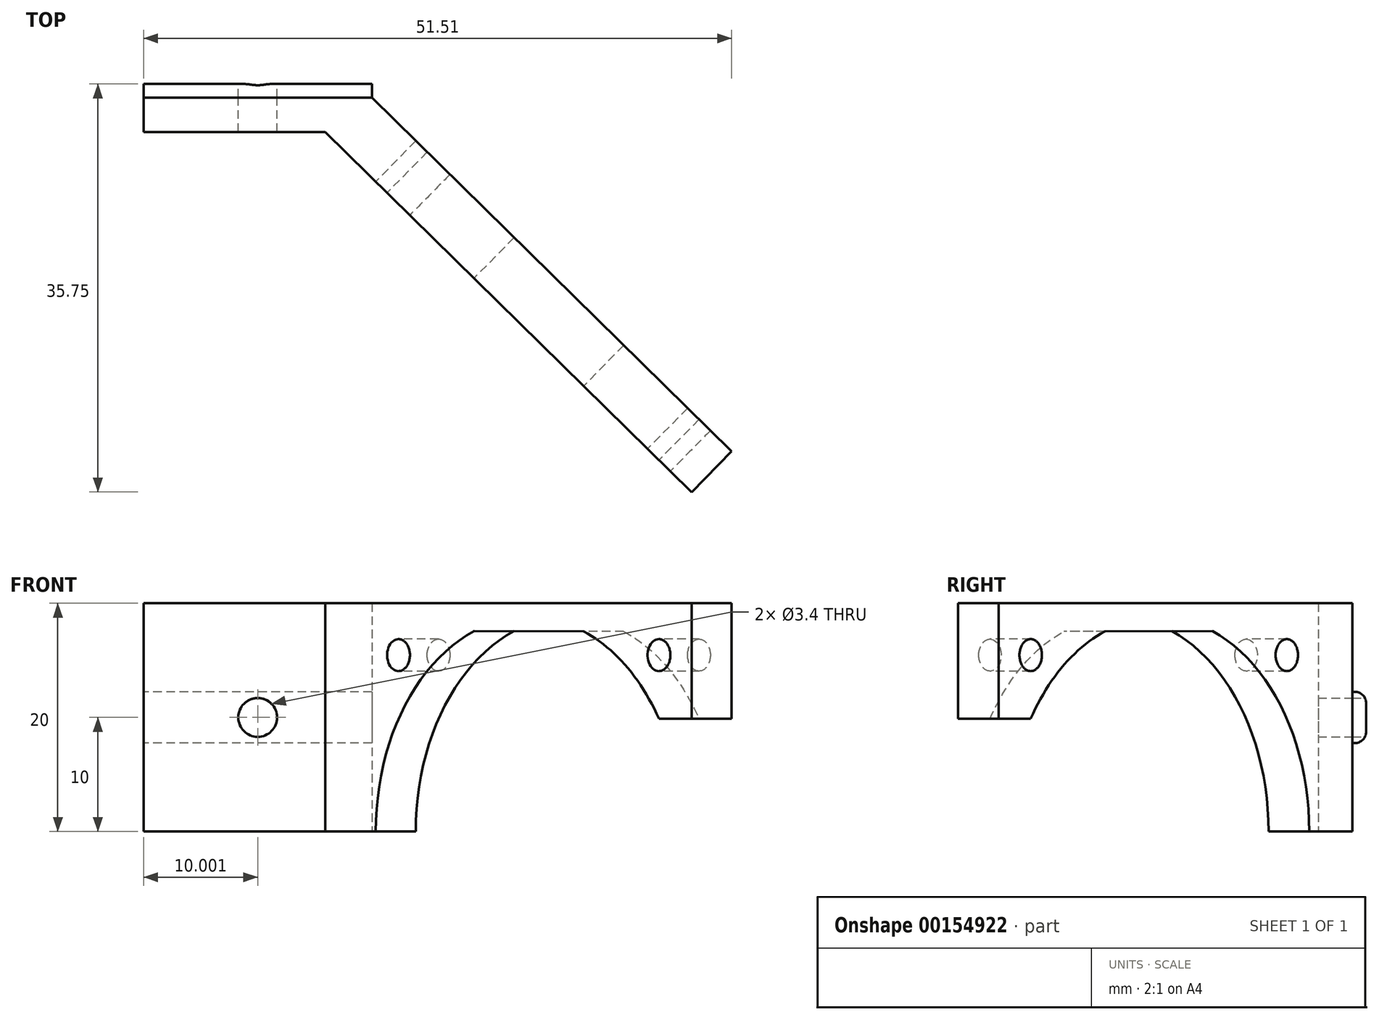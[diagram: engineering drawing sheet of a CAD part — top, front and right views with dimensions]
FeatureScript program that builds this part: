
annotation { "Feature Type Name" : "Feature", "Feature Type Description" : "" }
export const myFeature = defineFeature(function(context is Context, id is Id, definition is map)
    precondition{}
    {
        {
            var Q0;
            Q0=qCreatedBy(makeId("Top.planeOp"),FACE);
            var sketch = newSketch(context, id + "F0", { "sketchPlane" : qUnion([Q0])});
            skLineSegment(sketch, "E0", {"start": v(-32.55, 28) * mm, "end": v(-16.63, 28) * mm});
            skLineSegment(sketch, "E1", {"start": v(15.45, -3.56) * mm, "end": v(-16.63, 28) * mm});
            skLineSegment(sketch, "E2", {"start": v(15.45, -3.56) * mm, "end": v(18.96, 0) * mm});
            skLineSegment(sketch, "E3", {"start": v(-12.55, 31) * mm, "end": v(18.96, 0) * mm});
            skLineSegment(sketch, "E4", {"start": v(-12.55, 31) * mm, "end": v(-32.55, 31) * mm});
            skLineSegment(sketch, "E5", {"start": v(-32.55, 31) * mm, "end": v(-32.55, 28) * mm});
            skSolve(sketch);
        }
        {
            var Q0;
            Q0=makeQuery(id+"F0.imprint","IMPRINT",FACE,{"disambiguationData":[TD([[makeQuery(id+"F0.imprint","IMPRINT",EDGE,{"derivedFrom":sQuery(id+"F0.wireOp",EDGE,"E0")}),1.0]])]});
            extrude(context, id + "F1", {"entities" : qUnion([Q0]), "depth" : 20 * mm});
        }
        {
            var Q0;
            Q0=makeQuery(id+"F1.opExtrude","SWEPT_FACE",FACE,{"disambiguationData":[OSD([sQuery(id+"F0.wireOp",EDGE,"E5")])]});
            var sketch = newSketch(context, id + "F2", { "sketchPlane" : qUnion([Q0])});
            skLineSegment(sketch, "E6", {"start": v(-31, 12.25) * mm, "end": v(-31.2, 12.25) * mm});
            skLineSegment(sketch, "E7", {"start": v(-32.2, 11.25) * mm, "end": v(-32.2, 8.75) * mm});
            skLineSegment(sketch, "E8", {"start": v(-31.2, 7.75) * mm, "end": v(-31, 7.75) * mm});
            skLineSegment(sketch, "E9", {"start": v(-31, 7.75) * mm, "end": v(-31, 12.25) * mm});
            skPoint(sketch, "E10.visualSharp", {"position": v(-32.2, 12.25) * mm});
            skArc(sketch, "E10.filletArc", {"start": v(-31.2, 12.25) * mm, "mid": v(-31.9, 11.96) * mm, "end": v(-32.2, 11.25) * mm});
            skPoint(sketch, "E11.visualSharp", {"position": v(-32.2, 7.75) * mm});
            skArc(sketch, "E11.filletArc", {"start": v(-32.2, 8.75) * mm, "mid": v(-31.9, 8.04) * mm, "end": v(-31.2, 7.75) * mm});
            skPoint(sketch, "E12", {"position": v(-31, 10) * mm});
            skSolve(sketch);
        }
        {
            var Q0;
            Q0=makeQuery(id+"F2.imprint","IMPRINT",FACE,{"disambiguationData":[TD([[makeQuery(id+"F2.imprint","IMPRINT",EDGE,{"derivedFrom":sQuery(id+"F2.wireOp",EDGE,"E6")}),1.0]])]});
            extrude(context, id + "F3", {"entities" : qUnion([Q0]), "oppositeDirection" : true, "depth" : 20 * mm});
        }
        {
            var Q0;
            Q0=makeQuery(id+"F3.opExtrude","SWEPT_FACE",FACE,{"disambiguationData":[OSD([sQuery(id+"F2.wireOp",EDGE,"E7")])]});
            var sketch = newSketch(context, id + "F4", { "sketchPlane" : qUnion([Q0])});
            skPoint(sketch, "E13", {"position": v(22.55, 10) * mm});
            skPoint(sketch, "E13.positionSnap0", {"position": v(12.55, 10) * mm});
            skSolve(sketch);
        }
        {
            var Q0;
            Q0=sQuery(id+"F4.wireOp",VERTEX,"E13");
            var Q1;
            Q1=makeQuery(id+"F3.opExtrude","SWEPT_BODY",BODY,{"disambiguationData":[OSD([sQuery(id+"F2.wireOp",EDGE,"E6"),sQuery(id+"F2.wireOp",EDGE,"E7"),sQuery(id+"F2.wireOp",EDGE,"E8"),sQuery(id+"F2.wireOp",EDGE,"E9"),sQuery(id+"F2.wireOp",EDGE,"E10.filletArc"),sQuery(id+"F2.wireOp",EDGE,"E11.filletArc")])]});
            var Q2;
            Q2=makeQuery(id+"F1.opExtrude","SWEPT_BODY",BODY,{"disambiguationData":[OSD([sQuery(id+"F0.wireOp",EDGE,"E0"),sQuery(id+"F0.wireOp",EDGE,"E1"),sQuery(id+"F0.wireOp",EDGE,"E2"),sQuery(id+"F0.wireOp",EDGE,"E3"),sQuery(id+"F0.wireOp",EDGE,"E4"),sQuery(id+"F0.wireOp",EDGE,"E5")])]});
            hole(context, id + "F5", {"style" : HoleStyle.SIMPLE, "endStyle" : HoleEndStyle.THROUGH, "holeDiameter" : 3.4 * mm, "locations" : qUnion([Q0]), "scope" : qUnion([Q1, Q2]), "isTappedThrough" : true});
        }
        {
            var Q0;
            Q0=makeQuery(id+"F1.opExtrude","SWEPT_FACE",FACE,{"disambiguationData":[OSD([sQuery(id+"F0.wireOp",EDGE,"E1")])]});
            var sketch = newSketch(context, id + "F6", { "sketchPlane" : qUnion([Q0])});
            skLineSegment(sketch, "E14.bottom", {"start": v(13.52, 20) * mm, "end": v(-26.48, 20) * mm});
            skLineSegment(sketch, "E14.top", {"start": v(13.52, -20) * mm, "end": v(-26.48, -20) * mm});
            skLineSegment(sketch, "E14.left", {"start": v(13.52, 20) * mm, "end": v(13.52, -20) * mm});
            skLineSegment(sketch, "E14.right", {"start": v(-26.48, 20) * mm, "end": v(-26.48, -20) * mm});
            skLineSegment(sketch, "E15.bottom", {"start": v(9.52, 15.46) * mm, "end": v(-22.48, 15.46) * mm});
            skLineSegment(sketch, "E15.top", {"start": v(9.52, -15.46) * mm, "end": v(-22.48, -15.46) * mm});
            skLineSegment(sketch, "E15.left", {"start": v(9.52, 15.46) * mm, "end": v(9.52, -15.46) * mm});
            skLineSegment(sketch, "E15.right", {"start": v(-22.48, 15.46) * mm, "end": v(-22.48, -15.46) * mm});
            skPoint(sketch, "E15.middle", {"position": v(-6.48, 0) * mm});
            skPoint(sketch, "E15.middle.positionSnap0", {"position": v(-6.48, 20) * mm});
            skPoint(sketch, "E15.middle.positionSnap1", {"position": v(-26.48, 0) * mm});
            skPoint(sketch, "E15.centerSnap0", {"position": v(-6.48, 20) * mm});
            skPoint(sketch, "E15.centerSnap1", {"position": v(-26.48, 0) * mm});
            skCircle(sketch, "E16", {"center": v(-6.48, 0) * mm, "radius": 18.8 * mm});
            skLineSegment(sketch, "E17", {"start": v(9.52, 9.87) * mm, "end": v(13.52, 9.87) * mm});
            skLineSegment(sketch, "E18", {"start": v(-13.2, 17.56) * mm, "end": v(0.23, 17.56) * mm});
            skSolve(sketch);
        }
        {
            var Q0;
            Q0=sQuery(id+"F6.wireOp",VERTEX,"E15.bottom.end");
            var Q1;
            Q1=sQuery(id+"F6.wireOp",VERTEX,"E15.left.start");
            var Q2;
            Q2=makeQuery(id+"F1.opExtrude","SWEPT_BODY",BODY,{"disambiguationData":[OSD([sQuery(id+"F0.wireOp",EDGE,"E0"),sQuery(id+"F0.wireOp",EDGE,"E1"),sQuery(id+"F0.wireOp",EDGE,"E2"),sQuery(id+"F0.wireOp",EDGE,"E3"),sQuery(id+"F0.wireOp",EDGE,"E4"),sQuery(id+"F0.wireOp",EDGE,"E5")])]});
            hole(context, id + "F7", {"style" : HoleStyle.SIMPLE, "endStyle" : HoleEndStyle.THROUGH, "holeDiameter" : 2.8 * mm, "locations" : qUnion([Q0, Q1]), "scope" : qUnion([Q2]), "isTappedThrough" : true});
        }
        {
            var Q0;
            Q0=makeQuery(id+"F1.opExtrude","SWEPT_FACE",FACE,{"disambiguationData":[OSD([sQuery(id+"F0.wireOp",EDGE,"E1")])]});
            var sketch = newSketch(context, id + "F8", { "sketchPlane" : qUnion([Q0])});
            skLineSegment(sketch, "E19.bottom", {"start": v(13.52, 20) * mm, "end": v(-26.48, 20) * mm});
            skLineSegment(sketch, "E19.top", {"start": v(13.52, -20) * mm, "end": v(-26.48, -20) * mm});
            skLineSegment(sketch, "E19.left", {"start": v(13.52, 20) * mm, "end": v(13.52, -20) * mm});
            skLineSegment(sketch, "E19.right", {"start": v(-26.48, 20) * mm, "end": v(-26.48, -20) * mm});
            skLineSegment(sketch, "E20.bottom", {"start": v(9.52, 15.46) * mm, "end": v(-22.48, 15.46) * mm});
            skLineSegment(sketch, "E20.top", {"start": v(9.52, -15.46) * mm, "end": v(-22.48, -15.46) * mm});
            skLineSegment(sketch, "E20.left", {"start": v(9.52, 15.46) * mm, "end": v(9.52, -15.46) * mm});
            skLineSegment(sketch, "E20.right", {"start": v(-22.48, 15.46) * mm, "end": v(-22.48, -15.46) * mm});
            skPoint(sketch, "E20.middle", {"position": v(-6.48, 0) * mm});
            skPoint(sketch, "E20.middle.positionSnap0", {"position": v(-6.48, 20) * mm});
            skPoint(sketch, "E20.middle.positionSnap1", {"position": v(-26.48, 0) * mm});
            skPoint(sketch, "E20.centerSnap0", {"position": v(-6.48, 20) * mm});
            skPoint(sketch, "E20.centerSnap1", {"position": v(-26.48, 0) * mm});
            skCircle(sketch, "E21", {"center": v(-6.48, 0) * mm, "radius": 18.8 * mm});
            skLineSegment(sketch, "E22", {"start": v(9.52, 9.87) * mm, "end": v(13.52, 9.87) * mm});
            skLineSegment(sketch, "E23", {"start": v(-13.2, 17.56) * mm, "end": v(0.26, 17.55) * mm});
            skSolve(sketch);
        }
        {
            var Q0;
            {var subQ0=sQuery(id+"F8.wireOp",EDGE,"E21");var subQ3=sQuery(id+"F8.wireOp",EDGE,"E20.bottom");var subQ4=makeQuery(id+"F8.imprint","INTERSECT",VERTEX,{"disambiguationData":[OD(0.0)],"derivedFrom":[subQ3,subQ0]});Q0=makeQuery(id+"F8.imprint","IMPRINT",FACE,{"disambiguationData":[TD([[makeQuery(id+"F8.imprint","IMPRINT",EDGE,{"disambiguationData":[TD([[subQ4,-1.0]])],"derivedFrom":subQ3}),1.0]])]});}
            var Q1;
            {var subQ4=sQuery(id+"F8.wireOp",EDGE,"E23");Q1=makeQuery(id+"F8.imprint","IMPRINT",FACE,{"disambiguationData":[TD([[makeQuery(id+"F8.imprint","IMPRINT",EDGE,{"derivedFrom":subQ4}),-1.0]])]});}
            var Q2;
            {var subQ0=sQuery(id+"F8.wireOp",EDGE,"E21");var subQ1=sQuery(id+"F8.wireOp",EDGE,"E20.right");var subQ2=makeQuery(id+"F8.imprint","INTERSECT",VERTEX,{"disambiguationData":[OD(0.0)],"derivedFrom":[subQ1,subQ0]});Q2=makeQuery(id+"F8.imprint","IMPRINT",FACE,{"disambiguationData":[TD([[makeQuery(id+"F8.imprint","IMPRINT",EDGE,{"disambiguationData":[TD([[subQ2,-1.0]])],"derivedFrom":subQ1}),-1.0]])]});}
            var Q3;
            {var subQ1=sQuery(id+"F8.wireOp",EDGE,"E20.left");var subQ3=makeQuery(id+"F1.opExtrude","CAP_EDGE",EDGE,{"disambiguationData":[OSD([sQuery(id+"F0.wireOp",EDGE,"E1")])],"isStart":true});var subQ4=makeQuery(id+"F8.imprint","INTERSECT",VERTEX,{"derivedFrom":[subQ3,subQ1]});Q3=makeQuery(id+"F8.imprint","IMPRINT",FACE,{"disambiguationData":[TD([[makeQuery(id+"F8.imprint","IMPRINT",EDGE,{"disambiguationData":[TD([[subQ4,1.0]])],"derivedFrom":subQ3}),-1.0]])]});}
            var Q4;
            {var subQ0=sQuery(id+"F8.wireOp",EDGE,"E22");Q4=makeQuery(id+"F8.imprint","IMPRINT",FACE,{"disambiguationData":[TD([[makeQuery(id+"F8.imprint","IMPRINT",EDGE,{"derivedFrom":subQ0}),-1.0]])]});}
            extrude(context, id + "F9", {"entities" : qUnion([Q0, Q1, Q2, Q3, Q4]), "operationType" : NewBodyOperationType.REMOVE, "endBound" : BoundingType.THROUGH_ALL, "oppositeDirection" : true, "depth" : 25 * mm});
        }
    });
